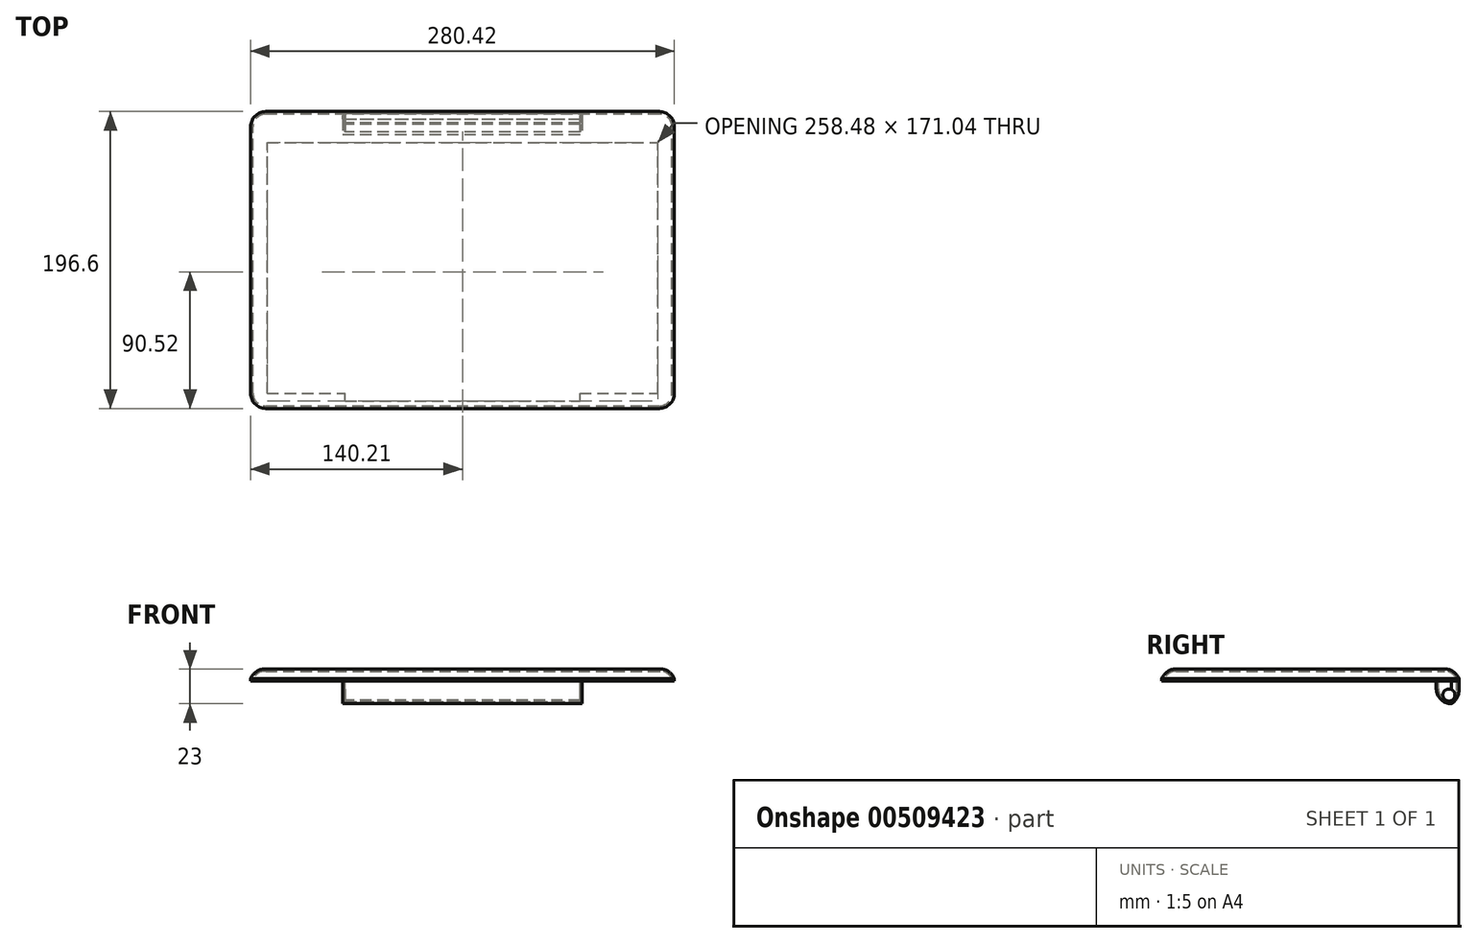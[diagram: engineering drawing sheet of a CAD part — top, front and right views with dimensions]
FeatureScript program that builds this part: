
annotation { "Feature Type Name" : "Feature", "Feature Type Description" : "" }
export const myFeature = defineFeature(function(context is Context, id is Id, definition is map)
    precondition{}
    {
        {
            var Q0;
            Q0=qCreatedBy(makeId("Top.planeOp"),FACE);
            var sketch = newSketch(context, id + "F0", { "sketchPlane" : qUnion([Q0])});
            skLineSegment(sketch, "E0.bottom", {"start": v(130.2, -98.3) * mm, "end": v(-130.2, -98.3) * mm});
            skLineSegment(sketch, "E0.top", {"start": v(130.2, 98.3) * mm, "end": v(-130.2, 98.3) * mm});
            skLineSegment(sketch, "E0.left", {"start": v(140.2, -88.3) * mm, "end": v(140.2, 88.3) * mm});
            skLineSegment(sketch, "E0.right", {"start": v(-140.2, -88.3) * mm, "end": v(-140.2, 88.3) * mm});
            skPoint(sketch, "E0.middle", {"position": v(0, 0) * mm});
            skPoint(sketch, "E1.visualSharp", {"position": v(-140.2, 98.3) * mm});
            skArc(sketch, "E1.filletArc", {"start": v(-130.2, 98.3) * mm, "mid": v(-137.28, 95.37) * mm, "end": v(-140.2, 88.3) * mm});
            skPoint(sketch, "E2.visualSharp", {"position": v(140.2, 98.3) * mm});
            skArc(sketch, "E2.filletArc", {"start": v(140.2, 88.3) * mm, "mid": v(137.28, 95.37) * mm, "end": v(130.2, 98.3) * mm});
            skPoint(sketch, "E3.visualSharp", {"position": v(140.2, -98.3) * mm});
            skArc(sketch, "E3.filletArc", {"start": v(130.2, -98.3) * mm, "mid": v(137.28, -95.37) * mm, "end": v(140.2, -88.3) * mm});
            skPoint(sketch, "E4.visualSharp", {"position": v(-140.2, -98.3) * mm});
            skArc(sketch, "E4.filletArc", {"start": v(-140.2, -88.3) * mm, "mid": v(-137.28, -95.37) * mm, "end": v(-130.2, -98.3) * mm});
            skSolve(sketch);
        }
        {
            var Q0;
            Q0 = qSketchRegion(id + "F0", true);
            extrude(context, id + "F1", {"entities" : qUnion([Q0]), "depth" : 6.5 * mm, "offsetDistance" : 25 * mm});
        }
        {
            var Q0;
            Q0=makeQuery(id+"F1.opExtrude","CAP_FACE",FACE,{"disambiguationData":[OSD([sQuery(id+"F0.wireOp",EDGE,"E0.bottom"),sQuery(id+"F0.wireOp",EDGE,"E0.top"),sQuery(id+"F0.wireOp",EDGE,"E0.left"),sQuery(id+"F0.wireOp",EDGE,"E0.right"),sQuery(id+"F0.wireOp",EDGE,"E1.filletArc"),sQuery(id+"F0.wireOp",EDGE,"E2.filletArc"),sQuery(id+"F0.wireOp",EDGE,"E3.filletArc"),sQuery(id+"F0.wireOp",EDGE,"E4.filletArc")])],"isStart":false});
            fillet(context, id + "F2", {"entities" : qUnion([Q0]), "radius" : 10 * mm, "tangentPropagation" : true, "allowEdgeOverflow" : false});
        }
        {
            var Q0;
            Q0=makeQuery(id+"F1.opExtrude","CAP_FACE",FACE,{"disambiguationData":[OSD([sQuery(id+"F0.wireOp",EDGE,"E0.bottom"),sQuery(id+"F0.wireOp",EDGE,"E0.top"),sQuery(id+"F0.wireOp",EDGE,"E0.left"),sQuery(id+"F0.wireOp",EDGE,"E0.right"),sQuery(id+"F0.wireOp",EDGE,"E1.filletArc"),sQuery(id+"F0.wireOp",EDGE,"E2.filletArc"),sQuery(id+"F0.wireOp",EDGE,"E3.filletArc"),sQuery(id+"F0.wireOp",EDGE,"E4.filletArc")])],"isStart":true});
            shell(context, id + "F3", {"entities" : qUnion([Q0]), "thickness" : 1.5 * mm});
        }
        {
            var Q0;
            Q0=makeQuery(id+"F1.opExtrude","CAP_FACE",FACE,{"disambiguationData":[OSD([sQuery(id+"F0.wireOp",EDGE,"E0.bottom"),sQuery(id+"F0.wireOp",EDGE,"E0.top"),sQuery(id+"F0.wireOp",EDGE,"E0.left"),sQuery(id+"F0.wireOp",EDGE,"E0.right"),sQuery(id+"F0.wireOp",EDGE,"E1.filletArc"),sQuery(id+"F0.wireOp",EDGE,"E2.filletArc"),sQuery(id+"F0.wireOp",EDGE,"E3.filletArc"),sQuery(id+"F0.wireOp",EDGE,"E4.filletArc")])],"isStart":true});
            var sketch = newSketch(context, id + "F4", { "sketchPlane" : qUnion([Q0])});
            skLineSegment(sketch, "E5.bottom", {"start": v(-130.2, 98.3) * mm, "end": v(130.2, 98.3) * mm});
            skLineSegment(sketch, "E5.top", {"start": v(-130.2, -98.3) * mm, "end": v(130.2, -98.3) * mm});
            skLineSegment(sketch, "E5.left", {"start": v(-140.2, 88.3) * mm, "end": v(-140.2, -88.3) * mm});
            skLineSegment(sketch, "E5.right", {"start": v(140.2, 88.3) * mm, "end": v(140.2, -88.3) * mm});
            skPoint(sketch, "E5.middle", {"position": v(0, 0) * mm});
            skPoint(sketch, "E6.visualSharp", {"position": v(-140.2, 98.3) * mm});
            skArc(sketch, "E6.filletArc", {"start": v(-130.2, 98.3) * mm, "mid": v(-137.28, 95.37) * mm, "end": v(-140.2, 88.3) * mm});
            skPoint(sketch, "E7.visualSharp", {"position": v(140.2, 98.3) * mm});
            skArc(sketch, "E7.filletArc", {"start": v(140.2, 88.3) * mm, "mid": v(137.28, 95.37) * mm, "end": v(130.2, 98.3) * mm});
            skPoint(sketch, "E8.visualSharp", {"position": v(-140.2, -98.3) * mm});
            skArc(sketch, "E8.filletArc", {"start": v(-140.2, -88.3) * mm, "mid": v(-137.28, -95.37) * mm, "end": v(-130.2, -98.3) * mm});
            skPoint(sketch, "E9.visualSharp", {"position": v(140.2, -98.3) * mm});
            skArc(sketch, "E9.filletArc", {"start": v(130.2, -98.3) * mm, "mid": v(137.28, -95.37) * mm, "end": v(140.2, -88.3) * mm});
            skLineSegment(sketch, "E10.0", {"start": v(-130.2, 88.3) * mm, "end": v(130.2, 88.3) * mm});
            skLineSegment(sketch, "E11.0", {"start": v(-129.24, 88.3) * mm, "end": v(-129.24, -77.74) * mm});
            skLineSegment(sketch, "E12.0", {"start": v(129.24, 88.3) * mm, "end": v(129.24, -77.74) * mm});
            skLineSegment(sketch, "E13.0", {"start": v(-129.24, -77.74) * mm, "end": v(129.24, -77.74) * mm});
            skSolve(sketch);
        }
        {
            var Q0;
            Q0 = qSketchRegion(id + "F4", true);
            extrude(context, id + "F5", {"entities" : qUnion([Q0]), "depth" : 1.5 * mm, "offsetDistance" : 25 * mm});
        }
        {
            var Q0;
            Q0=makeQuery(id+"F5.opExtrude","CAP_FACE",FACE,{"disambiguationData":[OSD([sQuery(id+"F4.wireOp",EDGE,"E5.bottom"),sQuery(id+"F4.wireOp",EDGE,"E5.top"),sQuery(id+"F4.wireOp",EDGE,"E5.left"),sQuery(id+"F4.wireOp",EDGE,"E5.right"),sQuery(id+"F4.wireOp",EDGE,"E6.filletArc"),sQuery(id+"F4.wireOp",EDGE,"E7.filletArc"),sQuery(id+"F4.wireOp",EDGE,"E8.filletArc"),sQuery(id+"F4.wireOp",EDGE,"E9.filletArc"),sQuery(id+"F4.wireOp",EDGE,"E10.0"),sQuery(id+"F4.wireOp",EDGE,"E11.0"),sQuery(id+"F4.wireOp",EDGE,"E12.0"),sQuery(id+"F4.wireOp",EDGE,"E13.0")])],"isStart":false});
            var sketch = newSketch(context, id + "F6", { "sketchPlane" : qUnion([Q0])});
            skPoint(sketch, "E14", {"position": v(-79.2, -98.3) * mm});
            skPoint(sketch, "E15", {"position": v(79.2, -98.3) * mm});
            skLineSegment(sketch, "E16.top", {"start": v(-79.2, -83.3) * mm, "end": v(79.2, -83.3) * mm});
            skLineSegment(sketch, "E16.right", {"start": v(79.2, -93.3) * mm, "end": v(79.2, -83.3) * mm});
            skLineSegment(sketch, "E17", {"start": v(-79.2, -93.3) * mm, "end": v(-79.2, -83.3) * mm});
            skLineSegment(sketch, "E18", {"start": v(-79.2, -93.3) * mm, "end": v(79.2, -93.3) * mm});
            skSolve(sketch);
        }
        {
            var Q0;
            Q0 = qSketchRegion(id + "F6", true);
            extrude(context, id + "F7", {"entities" : qUnion([Q0]), "operationType" : NewBodyOperationType.ADD, "depth" : 15 * mm, "offsetDistance" : 25 * mm});
        }
        {
            var Q0;
            Q0=makeQuery(id+"F7.opExtrude","CAP_EDGE",EDGE,{"disambiguationData":[OSD([sQuery(id+"F6.wireOp",EDGE,"E16.top")])],"isStart":false});
            fillet(context, id + "F8", {"entities" : qUnion([Q0]), "radius" : 10 * mm, "tangentPropagation" : true, "allowEdgeOverflow" : false});
        }
        {
            var Q0;
            Q0=makeQuery(id+"F1.opExtrude","CAP_FACE",FACE,{"disambiguationData":[OSD([sQuery(id+"F0.wireOp",EDGE,"E0.bottom"),sQuery(id+"F0.wireOp",EDGE,"E0.top"),sQuery(id+"F0.wireOp",EDGE,"E0.left"),sQuery(id+"F0.wireOp",EDGE,"E0.right"),sQuery(id+"F0.wireOp",EDGE,"E1.filletArc"),sQuery(id+"F0.wireOp",EDGE,"E2.filletArc"),sQuery(id+"F0.wireOp",EDGE,"E3.filletArc"),sQuery(id+"F0.wireOp",EDGE,"E4.filletArc")])],"isStart":true});
            var sketch = newSketch(context, id + "F9", { "sketchPlane" : qUnion([Q0])});
            skLineSegment(sketch, "E19.top", {"start": v(-79.2, -83.3) * mm, "end": v(79.2, -83.3) * mm});
            skPoint(sketch, "E20", {"position": v(-79.2, -98.3) * mm});
            skPoint(sketch, "E21", {"position": v(79.2, -98.3) * mm});
            skLineSegment(sketch, "E22.bottom", {"start": v(-79.2, -98.3) * mm, "end": v(79.2, -98.3) * mm});
            skLineSegment(sketch, "E22.top", {"start": v(-79.2, -93.3) * mm, "end": v(79.2, -93.3) * mm});
            skLineSegment(sketch, "E22.left", {"start": v(-79.2, -98.3) * mm, "end": v(-79.2, -93.3) * mm});
            skLineSegment(sketch, "E22.right", {"start": v(79.2, -98.3) * mm, "end": v(79.2, -93.3) * mm});
            skSolve(sketch);
        }
        {
            var Q0;
            Q0 = qSketchRegion(id + "F9", true);
            extrude(context, id + "F10", {"entities" : qUnion([Q0]), "depth" : 16.5 * mm, "offsetDistance" : 25 * mm});
        }
        {
            var Q0;
            Q0=makeQuery(id+"F10.opExtrude","CAP_EDGE",EDGE,{"disambiguationData":[OSD([sQuery(id+"F9.wireOp",EDGE,"E22.bottom")])],"isStart":false});
            fillet(context, id + "F11", {"entities" : qUnion([Q0]), "radius" : 10 * mm, "tangentPropagation" : true, "allowEdgeOverflow" : false});
        }
        {
            var Q0;
            Q0=makeQuery(id+"F7.opExtrude","SWEPT_FACE",FACE,{"disambiguationData":[OSD([sQuery(id+"F6.wireOp",EDGE,"E18")])]});
            shell(context, id + "F12", {"entities" : qUnion([Q0]), "thickness" : 1.5 * mm});
        }
        {
            var Q0;
            Q0=makeQuery(id+"F10.opExtrude","SWEPT_FACE",FACE,{"disambiguationData":[OSD([sQuery(id+"F9.wireOp",EDGE,"E22.top")])]});
            shell(context, id + "F13", {"entities" : qUnion([Q0]), "thickness" : 1.5 * mm});
        }
        {
            var Q0;
            Q0=makeQuery(id+"F13.opShell","OFFSET_FACE",FACE,{"disambiguationData":[OSD([sQuery(id+"F9.wireOp",EDGE,"E22.bottom"),sQuery(id+"F9.wireOp",EDGE,"E22.top"),sQuery(id+"F9.wireOp",EDGE,"E22.left"),sQuery(id+"F9.wireOp",EDGE,"E22.right")])]});
            extrude(context, id + "F14", {"entities" : qUnion([Q0]), "operationType" : NewBodyOperationType.REMOVE, "oppositeDirection" : true, "depth" : 1.5 * mm, "offsetDistance" : 25 * mm});
        }
        {
            var Q0;
            Q0=makeQuery(id+"F7.opExtrude","SWEPT_FACE",FACE,{"disambiguationData":[OSD([sQuery(id+"F6.wireOp",EDGE,"E17")])]});
            var sketch = newSketch(context, id + "F15", { "sketchPlane" : qUnion([Q0])});
            skCircle(sketch, "E23", {"center": v(-91.7, -10.73) * mm, "radius": 4 * mm});
            skSolve(sketch);
        }
        {
            var Q0;
            Q0 = qSketchRegion(id + "F15", true);
            extrude(context, id + "F16", {"entities" : qUnion([Q0]), "operationType" : NewBodyOperationType.REMOVE, "oppositeDirection" : true, "depth" : 200 * mm, "offsetDistance" : 25 * mm});
        }
        {
            var Q0;
            Q0 = qSketchRegion(id + "F9", true);
            var Q1;
            Q1 = qConstructionFilter(qBodyType(qCreatedBy(id + "F9" ,EDGE), BodyType.WIRE), ConstructionObject.NO);
            extrude(context, id + "F17", {"entities" : qUnion([Q0]), "operationType" : NewBodyOperationType.REMOVE, "surfaceEntities" : qUnion([Q1]), "depth" : 1.5 * mm, "offsetDistance" : 25 * mm});
        }
        {
            var Q0;
            {var subQ1=sQuery(id+"F4.wireOp",EDGE,"E13.0");var subQ2=sQuery(id+"F4.wireOp",EDGE,"E12.0");var subQ3=sQuery(id+"F4.wireOp",EDGE,"E11.0");var subQ4=sQuery(id+"F4.wireOp",EDGE,"E10.0");var subQ5=sQuery(id+"F4.wireOp",EDGE,"E9.filletArc");var subQ6=sQuery(id+"F4.wireOp",EDGE,"E8.filletArc");var subQ7=sQuery(id+"F4.wireOp",EDGE,"E7.filletArc");var subQ8=sQuery(id+"F4.wireOp",EDGE,"E6.filletArc");var subQ9=sQuery(id+"F4.wireOp",EDGE,"E5.right");var subQ10=sQuery(id+"F4.wireOp",EDGE,"E5.left");var subQ11=sQuery(id+"F4.wireOp",EDGE,"E5.top");var subQ12=sQuery(id+"F4.wireOp",EDGE,"E5.bottom");Q0=makeQuery(id+"F17.boolean.opBoolean","SPLIT",FACE,{"disambiguationData":[TD([makeQuery(id+"F12.opShell","OFFSET_FACE",FACE,{"disambiguationData":[OSD([sQuery(id+"F6.wireOp",EDGE,"E16.right")])]})])],"derivedFrom":makeQuery(id+"F12.opShell","MERGE",FACE,{"derivedFrom":[makeQuery(id+"F5.opExtrude","CAP_FACE",FACE,{"disambiguationData":[OSD([subQ12,subQ11,subQ10,subQ9,subQ8,subQ7,subQ6,subQ5,subQ4,subQ3,subQ2,subQ1])],"isStart":true}),makeQuery(id+"F5.opExtrude","CAP_FACE",FACE,{"disambiguationData":[OSD([subQ12,subQ11,subQ10,subQ9,subQ8,subQ7,subQ6,subQ5,subQ4,subQ3,subQ2,subQ1])],"isStart":false})]})});}
            var sketch = newSketch(context, id + "F18", { "sketchPlane" : qUnion([Q0])});
            skLineSegment(sketch, "E24.bottom", {"start": v(-77.7, -93.3) * mm, "end": v(77.7, -93.3) * mm});
            skLineSegment(sketch, "E24.top", {"start": v(-77.7, -84.8) * mm, "end": v(77.7, -84.8) * mm});
            skLineSegment(sketch, "E24.left", {"start": v(-77.7, -93.3) * mm, "end": v(-77.7, -84.8) * mm});
            skLineSegment(sketch, "E24.right", {"start": v(77.7, -93.3) * mm, "end": v(77.7, -84.8) * mm});
            skSolve(sketch);
        }
        {
            var Q0;
            Q0 = qSketchRegion(id + "F18", true);
            extrude(context, id + "F19", {"entities" : qUnion([Q0]), "operationType" : NewBodyOperationType.REMOVE, "oppositeDirection" : true, "depth" : 1.5 * mm, "offsetDistance" : 25 * mm});
        }
    });
